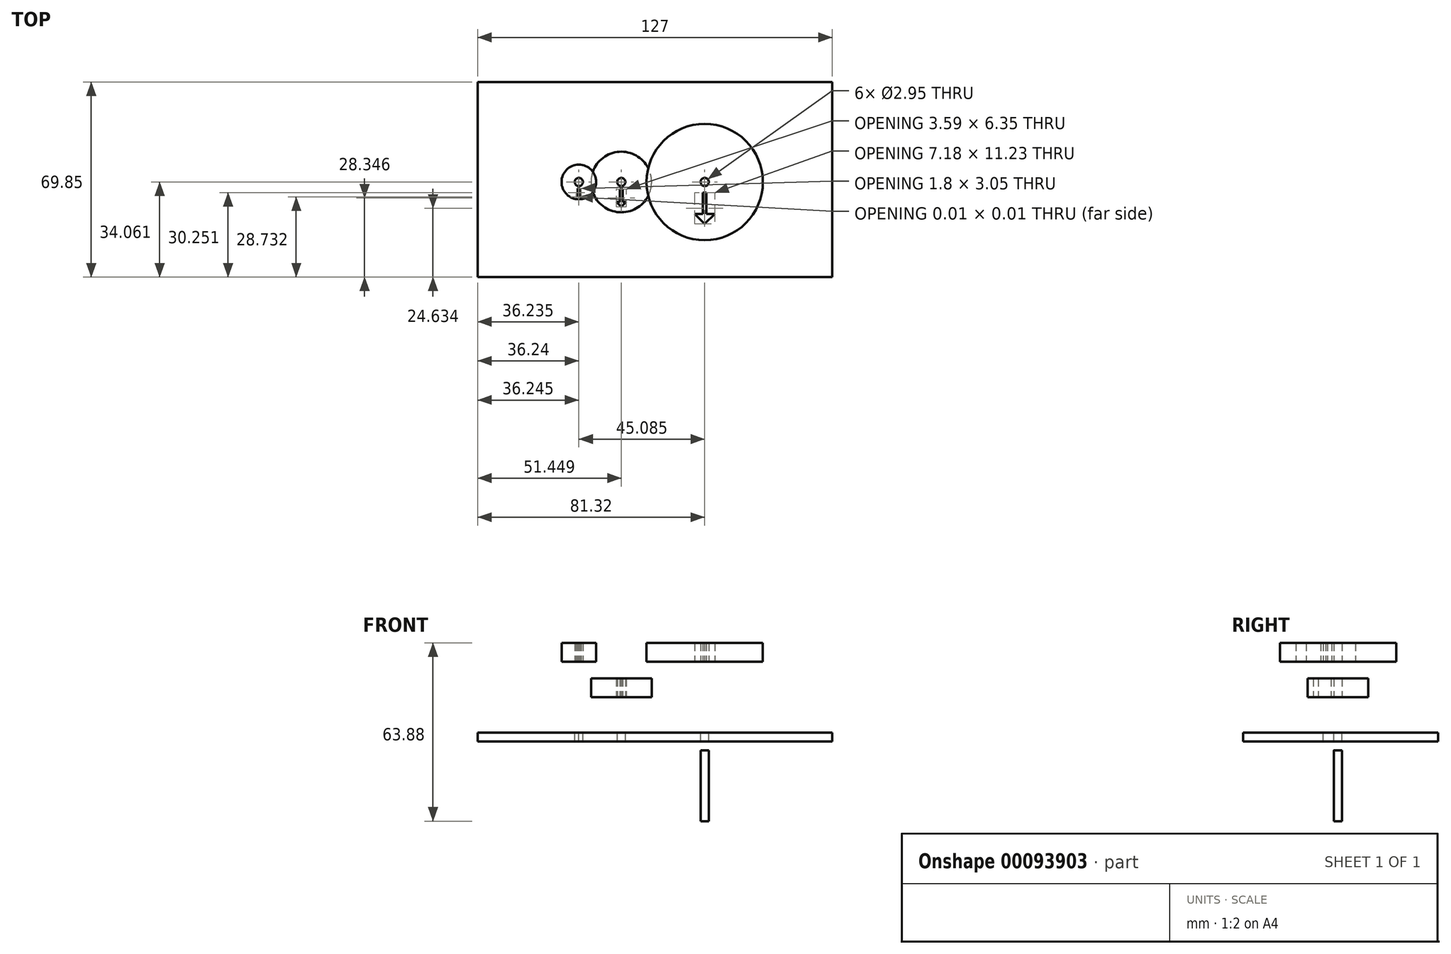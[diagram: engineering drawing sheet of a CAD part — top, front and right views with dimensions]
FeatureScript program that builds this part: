
annotation { "Feature Type Name" : "Feature", "Feature Type Description" : "" }
export const myFeature = defineFeature(function(context is Context, id is Id, definition is map)
    precondition{}
    {
        {
            var Q0;
            Q0=qCreatedBy(makeId("Top.planeOp"),FACE);
            var sketch = newSketch(context, id + "F0", { "sketchPlane" : qUnion([Q0])});
            skLineSegment(sketch, "E0", {"start": v(-33.34, 3.44) * mm, "end": v(-18.12, 3.44) * mm});
            skLineSegment(sketch, "E1", {"start": v(-18.12, 3.44) * mm, "end": v(11.75, 3.44) * mm});
            skCircle(sketch, "E2", {"center": v(-33.34, 3.44) * mm, "radius": 6.2 * mm});
            skCircle(sketch, "E3", {"center": v(11.75, 3.44) * mm, "radius": 20.84 * mm});
            skCircle(sketch, "E4", {"center": v(-18.12, 3.44) * mm, "radius": 10.86 * mm});
            skLineSegment(sketch, "E5.bottom", {"start": v(-69.57, 39.23) * mm, "end": v(57.43, 39.23) * mm});
            skLineSegment(sketch, "E5.top", {"start": v(-69.57, -30.62) * mm, "end": v(57.43, -30.62) * mm});
            skLineSegment(sketch, "E5.left", {"start": v(-69.57, 39.23) * mm, "end": v(-69.57, -30.62) * mm});
            skLineSegment(sketch, "E5.right", {"start": v(57.43, 39.23) * mm, "end": v(57.43, -30.62) * mm});
            skCircle(sketch, "E6", {"center": v(11.75, 3.44) * mm, "radius": 1.47 * mm});
            skCircle(sketch, "E7", {"center": v(-18.12, 3.44) * mm, "radius": 1.47 * mm});
            skCircle(sketch, "E8", {"center": v(-33.34, 3.44) * mm, "radius": 1.47 * mm});
            skLineSegment(sketch, "E9", {"start": v(11.75, 3.44) * mm, "end": v(11.75, -17.4) * mm});
            skLineSegment(sketch, "E10", {"start": v(11.11, -0.37) * mm, "end": v(11.11, -11.6) * mm});
            skLineSegment(sketch, "E11", {"start": v(11.11, -11.6) * mm, "end": v(12.38, -11.6) * mm});
            skLineSegment(sketch, "E12", {"start": v(11.11, -0.37) * mm, "end": v(12.38, -0.37) * mm});
            skLineSegment(sketch, "E13", {"start": v(12.38, -0.37) * mm, "end": v(12.38, -11.6) * mm});
            skLineSegment(sketch, "E14", {"start": v(11.75, -11.6) * mm, "end": v(15.34, -8) * mm});
            skLineSegment(sketch, "E15", {"start": v(11.75, -11.6) * mm, "end": v(8.16, -8) * mm});
            skLineSegment(sketch, "E16", {"start": v(8.16, -8) * mm, "end": v(15.34, -8) * mm});
            skLineSegment(sketch, "E17", {"start": v(-18.63, 0.9) * mm, "end": v(-18.63, -5.45) * mm});
            skLineSegment(sketch, "E18", {"start": v(-18.63, 0.9) * mm, "end": v(-17.61, 0.9) * mm});
            skLineSegment(sketch, "E19", {"start": v(-17.61, 0.9) * mm, "end": v(-17.61, -5.45) * mm});
            skLineSegment(sketch, "E20", {"start": v(-18.12, 3.44) * mm, "end": v(-18.12, -7.42) * mm});
            skLineSegment(sketch, "E21", {"start": v(-18.63, -5.45) * mm, "end": v(-17.61, -5.45) * mm});
            skLineSegment(sketch, "E22", {"start": v(-18.12, -5.45) * mm, "end": v(-16.32, -3.65) * mm});
            skLineSegment(sketch, "E23", {"start": v(-18.12, -5.45) * mm, "end": v(-19.92, -3.65) * mm});
            skLineSegment(sketch, "E24", {"start": v(-19.92, -3.65) * mm, "end": v(-16.32, -3.65) * mm});
            skLineSegment(sketch, "E25", {"start": v(-33.34, 3.44) * mm, "end": v(-33.34, -2.76) * mm});
            skLineSegment(sketch, "E26", {"start": v(-33.72, 1.15) * mm, "end": v(-32.95, 1.15) * mm});
            skLineSegment(sketch, "E27", {"start": v(-32.95, 1.15) * mm, "end": v(-32.95, -1.9) * mm});
            skLineSegment(sketch, "E28", {"start": v(-33.72, 1.15) * mm, "end": v(-33.72, -1.19) * mm});
            skLineSegment(sketch, "E29", {"start": v(-32.95, -1.9) * mm, "end": v(-33.7, -1.9) * mm});
            skLineSegment(sketch, "E30", {"start": v(-33.32, -1.9) * mm, "end": v(-32.43, -1) * mm});
            skLineSegment(sketch, "E31", {"start": v(-33.32, -1.9) * mm, "end": v(-34.22, -1) * mm});
            skLineSegment(sketch, "E32", {"start": v(-34.22, -1) * mm, "end": v(-32.43, -1) * mm});
            skSolve(sketch);
        }
        {
            var Q0;
            Q0=makeQuery(id+"F0.imprint","IMPRINT",FACE,{"disambiguationData":[TD([[makeQuery(id+"F0.imprint","IMPRINT",EDGE,{"derivedFrom":sQuery(id+"F0.wireOp",EDGE,"E5.bottom")}),-1.0]])]});
            var Q1;
            Q1=makeQuery(id+"F0.imprint","IMPRINT",FACE,{"disambiguationData":[TD([[makeQuery(id+"F0.imprint","IMPRINT",EDGE,{"derivedFrom":sQuery(id+"F0.wireOp",EDGE,"E6")}),-1.0]])]});
            var Q2;
            {var subQ6=sQuery(id+"F0.wireOp",EDGE,"E0");var subQ9=sQuery(id+"F0.wireOp",EDGE,"E2");var subQ10=makeQuery(id+"F0.imprint","INTERSECT",VERTEX,{"derivedFrom":[subQ6,subQ9]});Q2=makeQuery(id+"F0.imprint","IMPRINT",FACE,{"disambiguationData":[TD([[makeQuery(id+"F0.imprint","IMPRINT",EDGE,{"disambiguationData":[TD([[subQ10,-1.0]])],"derivedFrom":subQ6}),1.0]])]});}
            var Q3;
            Q3=makeQuery(id+"F0.imprint","IMPRINT",FACE,{"disambiguationData":[TD([[makeQuery(id+"F0.imprint","IMPRINT",EDGE,{"derivedFrom":sQuery(id+"F0.wireOp",EDGE,"E8")}),-1.0]])]});
            var Q4;
            {var subQ0=sQuery(id+"F0.wireOp",EDGE,"E4");var subQ1=sQuery(id+"F0.wireOp",EDGE,"E0");var subQ2=makeQuery(id+"F0.imprint","INTERSECT",VERTEX,{"derivedFrom":[subQ1,subQ0]});Q4=makeQuery(id+"F0.imprint","IMPRINT",FACE,{"disambiguationData":[TD([[makeQuery(id+"F0.imprint","IMPRINT",EDGE,{"disambiguationData":[TD([[subQ2,-1.0]])],"derivedFrom":subQ1}),-1.0]])]});}
            var Q5;
            {var subQ0=sQuery(id+"F0.wireOp",EDGE,"E4");var subQ1=sQuery(id+"F0.wireOp",EDGE,"E0");var subQ2=makeQuery(id+"F0.imprint","INTERSECT",VERTEX,{"derivedFrom":[subQ1,subQ0]});Q5=makeQuery(id+"F0.imprint","IMPRINT",FACE,{"disambiguationData":[TD([[makeQuery(id+"F0.imprint","IMPRINT",EDGE,{"disambiguationData":[TD([[subQ2,-1.0]])],"derivedFrom":subQ1}),1.0]])]});}
            var Q6;
            {var subQ0=sQuery(id+"F0.wireOp",EDGE,"E4");var subQ1=sQuery(id+"F0.wireOp",EDGE,"E1");var subQ2=makeQuery(id+"F0.imprint","INTERSECT",VERTEX,{"derivedFrom":[subQ1,subQ0]});Q6=makeQuery(id+"F0.imprint","IMPRINT",FACE,{"disambiguationData":[TD([[makeQuery(id+"F0.imprint","IMPRINT",EDGE,{"disambiguationData":[TD([[subQ2,1.0]])],"derivedFrom":subQ1}),-1.0]])]});}
            var Q7;
            {var subQ0=sQuery(id+"F0.wireOp",EDGE,"E4");var subQ1=sQuery(id+"F0.wireOp",EDGE,"E1");var subQ2=makeQuery(id+"F0.imprint","INTERSECT",VERTEX,{"derivedFrom":[subQ1,subQ0]});Q7=makeQuery(id+"F0.imprint","IMPRINT",FACE,{"disambiguationData":[TD([[makeQuery(id+"F0.imprint","IMPRINT",EDGE,{"disambiguationData":[TD([[subQ2,1.0]])],"derivedFrom":subQ1}),1.0]])]});}
            var Q8;
            {var subQ0=sQuery(id+"F0.wireOp",EDGE,"E26");var subQ1=sQuery(id+"F0.wireOp",EDGE,"E25");var subQ2=makeQuery(id+"F0.imprint","INTERSECT",VERTEX,{"derivedFrom":[subQ1,subQ0]});Q8=makeQuery(id+"F0.imprint","IMPRINT",FACE,{"disambiguationData":[TD([[makeQuery(id+"F0.imprint","IMPRINT",EDGE,{"disambiguationData":[TD([[subQ2,-1.0]])],"derivedFrom":subQ1}),-1.0]])]});}
            var Q9;
            {var subQ0=sQuery(id+"F0.wireOp",EDGE,"E32");var subQ1=sQuery(id+"F0.wireOp",EDGE,"E25");var subQ2=makeQuery(id+"F0.imprint","INTERSECT",VERTEX,{"derivedFrom":[subQ1,subQ0]});Q9=makeQuery(id+"F0.imprint","IMPRINT",FACE,{"disambiguationData":[TD([[makeQuery(id+"F0.imprint","IMPRINT",EDGE,{"disambiguationData":[TD([[subQ2,-1.0]])],"derivedFrom":subQ1}),-1.0]])]});}
            var Q10;
            {var subQ0=sQuery(id+"F0.wireOp",EDGE,"E26");var subQ1=sQuery(id+"F0.wireOp",EDGE,"E25");var subQ2=makeQuery(id+"F0.imprint","INTERSECT",VERTEX,{"derivedFrom":[subQ1,subQ0]});Q10=makeQuery(id+"F0.imprint","IMPRINT",FACE,{"disambiguationData":[TD([[makeQuery(id+"F0.imprint","IMPRINT",EDGE,{"disambiguationData":[TD([[subQ2,-1.0]])],"derivedFrom":subQ1}),1.0]])]});}
            var Q11;
            {var subQ5=sQuery(id+"F0.wireOp",EDGE,"E32");var subQ7=sQuery(id+"F0.wireOp",EDGE,"E25");var subQ9=makeQuery(id+"F0.imprint","INTERSECT",VERTEX,{"derivedFrom":[subQ7,subQ5]});Q11=makeQuery(id+"F0.imprint","IMPRINT",FACE,{"disambiguationData":[TD([[makeQuery(id+"F0.imprint","IMPRINT",EDGE,{"disambiguationData":[TD([[subQ9,-1.0]])],"derivedFrom":subQ7}),1.0]])]});}
            var Q12;
            {var subQ0=sQuery(id+"F0.wireOp",EDGE,"E32");var subQ1=sQuery(id+"F0.wireOp",EDGE,"E27");var subQ2=makeQuery(id+"F0.imprint","INTERSECT",VERTEX,{"derivedFrom":[subQ1,subQ0]});Q12=makeQuery(id+"F0.imprint","IMPRINT",FACE,{"disambiguationData":[TD([[makeQuery(id+"F0.imprint","IMPRINT",EDGE,{"disambiguationData":[TD([[subQ2,-1.0]])],"derivedFrom":subQ1}),1.0]])]});}
            var Q13;
            {var subQ0=sQuery(id+"F0.wireOp",EDGE,"E29");var subQ1=sQuery(id+"F0.wireOp",EDGE,"E27");var subQ2=makeQuery(id+"F0.imprint","INTERSECT",VERTEX,{"derivedFrom":[subQ1,subQ0]});Q13=makeQuery(id+"F0.imprint","IMPRINT",FACE,{"disambiguationData":[TD([[makeQuery(id+"F0.imprint","IMPRINT",EDGE,{"disambiguationData":[TD([[subQ2,1.0]])],"derivedFrom":subQ1}),-1.0]])]});}
            var Q14;
            {var subQ15=sQuery(id+"F0.wireOp",EDGE,"E8");var subQ20=sQuery(id+"F0.wireOp",EDGE,"E0");var subQ21=makeQuery(id+"F0.imprint","INTERSECT",VERTEX,{"derivedFrom":[subQ20,subQ15]});Q14=makeQuery(id+"F0.imprint","IMPRINT",FACE,{"disambiguationData":[TD([[makeQuery(id+"F0.imprint","IMPRINT",EDGE,{"disambiguationData":[TD([[subQ21,-1.0]])],"derivedFrom":subQ20}),-1.0]])]});}
            var Q15;
            {var subQ1=sQuery(id+"F0.wireOp",EDGE,"E7");var subQ15=sQuery(id+"F0.wireOp",EDGE,"E1");var subQ20=makeQuery(id+"F0.imprint","INTERSECT",VERTEX,{"derivedFrom":[subQ15,subQ1]});Q15=makeQuery(id+"F0.imprint","IMPRINT",FACE,{"disambiguationData":[TD([[makeQuery(id+"F0.imprint","IMPRINT",EDGE,{"disambiguationData":[TD([[subQ20,-1.0]])],"derivedFrom":subQ15}),-1.0]])]});}
            var Q16;
            {var subQ0=sQuery(id+"F0.wireOp",EDGE,"E18");var subQ1=sQuery(id+"F0.wireOp",EDGE,"E17");var subQ2=makeQuery(id+"F0.imprint","INTERSECT",VERTEX,{"derivedFrom":[subQ1,subQ0]});Q16=makeQuery(id+"F0.imprint","IMPRINT",FACE,{"disambiguationData":[TD([[makeQuery(id+"F0.imprint","IMPRINT",EDGE,{"disambiguationData":[TD([[subQ2,-1.0]])],"derivedFrom":subQ1}),1.0]])]});}
            var Q17;
            {var subQ0=sQuery(id+"F0.wireOp",EDGE,"E19");var subQ1=sQuery(id+"F0.wireOp",EDGE,"E18");var subQ2=makeQuery(id+"F0.imprint","INTERSECT",VERTEX,{"derivedFrom":[subQ1,subQ0]});Q17=makeQuery(id+"F0.imprint","IMPRINT",FACE,{"disambiguationData":[TD([[makeQuery(id+"F0.imprint","IMPRINT",EDGE,{"disambiguationData":[TD([[subQ2,1.0]])],"derivedFrom":subQ1}),-1.0]])]});}
            var Q18;
            {var subQ0=sQuery(id+"F0.wireOp",EDGE,"E24");var subQ1=sQuery(id+"F0.wireOp",EDGE,"E17");var subQ2=makeQuery(id+"F0.imprint","INTERSECT",VERTEX,{"derivedFrom":[subQ1,subQ0]});Q18=makeQuery(id+"F0.imprint","IMPRINT",FACE,{"disambiguationData":[TD([[makeQuery(id+"F0.imprint","IMPRINT",EDGE,{"disambiguationData":[TD([[subQ2,-1.0]])],"derivedFrom":subQ1}),-1.0]])]});}
            var Q19;
            {var subQ0=sQuery(id+"F0.wireOp",EDGE,"E24");var subQ1=sQuery(id+"F0.wireOp",EDGE,"E17");var subQ2=makeQuery(id+"F0.imprint","INTERSECT",VERTEX,{"derivedFrom":[subQ1,subQ0]});Q19=makeQuery(id+"F0.imprint","IMPRINT",FACE,{"disambiguationData":[TD([[makeQuery(id+"F0.imprint","IMPRINT",EDGE,{"disambiguationData":[TD([[subQ2,-1.0]])],"derivedFrom":subQ1}),1.0]])]});}
            var Q20;
            {var subQ0=sQuery(id+"F0.wireOp",EDGE,"E24");var subQ1=sQuery(id+"F0.wireOp",EDGE,"E19");var subQ2=makeQuery(id+"F0.imprint","INTERSECT",VERTEX,{"derivedFrom":[subQ1,subQ0]});Q20=makeQuery(id+"F0.imprint","IMPRINT",FACE,{"disambiguationData":[TD([[makeQuery(id+"F0.imprint","IMPRINT",EDGE,{"disambiguationData":[TD([[subQ2,-1.0]])],"derivedFrom":subQ1}),-1.0]])]});}
            var Q21;
            {var subQ0=sQuery(id+"F0.wireOp",EDGE,"E24");var subQ1=sQuery(id+"F0.wireOp",EDGE,"E19");var subQ2=makeQuery(id+"F0.imprint","INTERSECT",VERTEX,{"derivedFrom":[subQ1,subQ0]});Q21=makeQuery(id+"F0.imprint","IMPRINT",FACE,{"disambiguationData":[TD([[makeQuery(id+"F0.imprint","IMPRINT",EDGE,{"disambiguationData":[TD([[subQ2,-1.0]])],"derivedFrom":subQ1}),1.0]])]});}
            var Q22;
            {var subQ0=sQuery(id+"F0.wireOp",EDGE,"E21");var subQ1=sQuery(id+"F0.wireOp",EDGE,"E19");var subQ2=makeQuery(id+"F0.imprint","INTERSECT",VERTEX,{"derivedFrom":[subQ1,subQ0]});Q22=makeQuery(id+"F0.imprint","IMPRINT",FACE,{"disambiguationData":[TD([[makeQuery(id+"F0.imprint","IMPRINT",EDGE,{"disambiguationData":[TD([[subQ2,1.0]])],"derivedFrom":subQ1}),-1.0]])]});}
            var Q23;
            {var subQ0=sQuery(id+"F0.wireOp",EDGE,"E21");var subQ1=sQuery(id+"F0.wireOp",EDGE,"E17");var subQ2=makeQuery(id+"F0.imprint","INTERSECT",VERTEX,{"derivedFrom":[subQ1,subQ0]});Q23=makeQuery(id+"F0.imprint","IMPRINT",FACE,{"disambiguationData":[TD([[makeQuery(id+"F0.imprint","IMPRINT",EDGE,{"disambiguationData":[TD([[subQ2,1.0]])],"derivedFrom":subQ1}),1.0]])]});}
            var Q24;
            {var subQ7=sQuery(id+"F0.wireOp",EDGE,"E2");var subQ8=sQuery(id+"F0.wireOp",EDGE,"E0");var subQ9=makeQuery(id+"F0.imprint","INTERSECT",VERTEX,{"derivedFrom":[subQ8,subQ7]});Q24=makeQuery(id+"F0.imprint","IMPRINT",FACE,{"disambiguationData":[TD([[makeQuery(id+"F0.imprint","IMPRINT",EDGE,{"disambiguationData":[TD([[subQ9,-1.0]])],"derivedFrom":subQ8}),-1.0]])]});}
            var Q25;
            {var subQ3=sQuery(id+"F0.wireOp",EDGE,"E16");var subQ5=sQuery(id+"F0.wireOp",EDGE,"E13");var subQ6=makeQuery(id+"F0.imprint","INTERSECT",VERTEX,{"derivedFrom":[subQ5,subQ3]});Q25=makeQuery(id+"F0.imprint","IMPRINT",FACE,{"disambiguationData":[TD([[makeQuery(id+"F0.imprint","IMPRINT",EDGE,{"disambiguationData":[TD([[subQ6,-1.0]])],"derivedFrom":subQ5}),-1.0]])]});}
            var Q26;
            {var subQ0=sQuery(id+"F0.wireOp",EDGE,"E16");var subQ1=sQuery(id+"F0.wireOp",EDGE,"E13");var subQ2=makeQuery(id+"F0.imprint","INTERSECT",VERTEX,{"derivedFrom":[subQ1,subQ0]});Q26=makeQuery(id+"F0.imprint","IMPRINT",FACE,{"disambiguationData":[TD([[makeQuery(id+"F0.imprint","IMPRINT",EDGE,{"disambiguationData":[TD([[subQ2,-1.0]])],"derivedFrom":subQ1}),1.0]])]});}
            var Q27;
            {var subQ3=sQuery(id+"F0.wireOp",EDGE,"E16");var subQ5=sQuery(id+"F0.wireOp",EDGE,"E10");var subQ7=makeQuery(id+"F0.imprint","INTERSECT",VERTEX,{"derivedFrom":[subQ5,subQ3]});Q27=makeQuery(id+"F0.imprint","IMPRINT",FACE,{"disambiguationData":[TD([[makeQuery(id+"F0.imprint","IMPRINT",EDGE,{"disambiguationData":[TD([[subQ7,-1.0]])],"derivedFrom":subQ5}),1.0]])]});}
            var Q28;
            {var subQ0=sQuery(id+"F0.wireOp",EDGE,"E16");var subQ1=sQuery(id+"F0.wireOp",EDGE,"E10");var subQ2=makeQuery(id+"F0.imprint","INTERSECT",VERTEX,{"derivedFrom":[subQ1,subQ0]});Q28=makeQuery(id+"F0.imprint","IMPRINT",FACE,{"disambiguationData":[TD([[makeQuery(id+"F0.imprint","IMPRINT",EDGE,{"disambiguationData":[TD([[subQ2,-1.0]])],"derivedFrom":subQ1}),-1.0]])]});}
            var Q29;
            {var subQ0=sQuery(id+"F0.wireOp",EDGE,"E12");var subQ1=sQuery(id+"F0.wireOp",EDGE,"E9");var subQ2=makeQuery(id+"F0.imprint","INTERSECT",VERTEX,{"derivedFrom":[subQ1,subQ0]});Q29=makeQuery(id+"F0.imprint","IMPRINT",FACE,{"disambiguationData":[TD([[makeQuery(id+"F0.imprint","IMPRINT",EDGE,{"disambiguationData":[TD([[subQ2,-1.0]])],"derivedFrom":subQ1}),1.0]])]});}
            var Q30;
            {var subQ0=sQuery(id+"F0.wireOp",EDGE,"E12");var subQ1=sQuery(id+"F0.wireOp",EDGE,"E9");var subQ2=makeQuery(id+"F0.imprint","INTERSECT",VERTEX,{"derivedFrom":[subQ1,subQ0]});Q30=makeQuery(id+"F0.imprint","IMPRINT",FACE,{"disambiguationData":[TD([[makeQuery(id+"F0.imprint","IMPRINT",EDGE,{"disambiguationData":[TD([[subQ2,-1.0]])],"derivedFrom":subQ1}),-1.0]])]});}
            var Q31;
            {var subQ0=sQuery(id+"F0.wireOp",EDGE,"E13");var subQ1=sQuery(id+"F0.wireOp",EDGE,"E11");var subQ2=makeQuery(id+"F0.imprint","INTERSECT",VERTEX,{"derivedFrom":[subQ1,subQ0]});Q31=makeQuery(id+"F0.imprint","IMPRINT",FACE,{"disambiguationData":[TD([[makeQuery(id+"F0.imprint","IMPRINT",EDGE,{"disambiguationData":[TD([[subQ2,1.0]])],"derivedFrom":subQ0}),-1.0]])]});}
            var Q32;
            {var subQ0=sQuery(id+"F0.wireOp",EDGE,"E11");var subQ1=sQuery(id+"F0.wireOp",EDGE,"E10");var subQ2=makeQuery(id+"F0.imprint","INTERSECT",VERTEX,{"derivedFrom":[subQ1,subQ0]});Q32=makeQuery(id+"F0.imprint","IMPRINT",FACE,{"disambiguationData":[TD([[makeQuery(id+"F0.imprint","IMPRINT",EDGE,{"disambiguationData":[TD([[subQ2,1.0]])],"derivedFrom":subQ1}),1.0]])]});}
            extrude(context, id + "F1", {"entities" : qUnion([Q0, Q1, Q2, Q3, Q4, Q5, Q6, Q7, Q8, Q9, Q10, Q11, Q12, Q13, Q14, Q15, Q16, Q17, Q18, Q19, Q20, Q21, Q22, Q23, Q24, Q25, Q26, Q27, Q28, Q29, Q30, Q31, Q32]), "oppositeDirection" : true, "depth" : 3.17 * mm});
        }
        {
            var Q0;
            {var subQ7=sQuery(id+"F0.wireOp",EDGE,"E4");var subQ8=sQuery(id+"F0.wireOp",EDGE,"E1");var subQ9=makeQuery(id+"F0.imprint","INTERSECT",VERTEX,{"derivedFrom":[subQ8,subQ7]});Q0=makeQuery(id+"F0.imprint","IMPRINT",FACE,{"disambiguationData":[TD([[makeQuery(id+"F0.imprint","IMPRINT",EDGE,{"disambiguationData":[TD([[subQ9,-1.0]])],"derivedFrom":subQ8}),-1.0]])]});}
            var Q1;
            {var subQ0=sQuery(id+"F0.wireOp",EDGE,"E3");var subQ1=sQuery(id+"F0.wireOp",EDGE,"E1");var subQ2=makeQuery(id+"F0.imprint","INTERSECT",VERTEX,{"derivedFrom":[subQ1,subQ0]});Q1=makeQuery(id+"F0.imprint","IMPRINT",FACE,{"disambiguationData":[TD([[makeQuery(id+"F0.imprint","IMPRINT",EDGE,{"disambiguationData":[TD([[subQ2,-1.0]])],"derivedFrom":subQ1}),-1.0]])]});}
            var Q2;
            {var subQ0=sQuery(id+"F0.wireOp",EDGE,"E3");var subQ1=sQuery(id+"F0.wireOp",EDGE,"E1");var subQ2=makeQuery(id+"F0.imprint","INTERSECT",VERTEX,{"derivedFrom":[subQ1,subQ0]});Q2=makeQuery(id+"F0.imprint","IMPRINT",FACE,{"disambiguationData":[TD([[makeQuery(id+"F0.imprint","IMPRINT",EDGE,{"disambiguationData":[TD([[subQ2,-1.0]])],"derivedFrom":subQ1}),1.0]])]});}
            var Q3;
            {var subQ0=sQuery(id+"F0.wireOp",EDGE,"E13");var subQ1=sQuery(id+"F0.wireOp",EDGE,"E11");var subQ2=makeQuery(id+"F0.imprint","INTERSECT",VERTEX,{"derivedFrom":[subQ1,subQ0]});Q3=makeQuery(id+"F0.imprint","IMPRINT",FACE,{"disambiguationData":[TD([[makeQuery(id+"F0.imprint","IMPRINT",EDGE,{"disambiguationData":[TD([[subQ2,1.0]])],"derivedFrom":subQ0}),-1.0]])]});}
            var Q4;
            {var subQ0=sQuery(id+"F0.wireOp",EDGE,"E11");var subQ1=sQuery(id+"F0.wireOp",EDGE,"E10");var subQ2=makeQuery(id+"F0.imprint","INTERSECT",VERTEX,{"derivedFrom":[subQ1,subQ0]});Q4=makeQuery(id+"F0.imprint","IMPRINT",FACE,{"disambiguationData":[TD([[makeQuery(id+"F0.imprint","IMPRINT",EDGE,{"disambiguationData":[TD([[subQ2,1.0]])],"derivedFrom":subQ1}),1.0]])]});}
            var Q5;
            {var subQ15=sQuery(id+"F0.wireOp",EDGE,"E4");var subQ16=sQuery(id+"F0.wireOp",EDGE,"E1");var subQ17=makeQuery(id+"F0.imprint","INTERSECT",VERTEX,{"derivedFrom":[subQ16,subQ15]});Q5=makeQuery(id+"F0.imprint","IMPRINT",FACE,{"disambiguationData":[TD([[makeQuery(id+"F0.imprint","IMPRINT",EDGE,{"disambiguationData":[TD([[subQ17,-1.0]])],"derivedFrom":subQ16}),1.0]])]});}
            extrude(context, id + "F2", {"entities" : qUnion([Q0, Q1, Q2, Q3, Q4, Q5]), "depth" : 32.13 * mm, "hasSecondDirection" : true, "secondDirectionOppositeDirection" : false, "secondDirectionDepth" : 25.4 * mm});
        }
        {
            var Q0;
            {var subQ0=sQuery(id+"F0.wireOp",EDGE,"E4");var subQ1=sQuery(id+"F0.wireOp",EDGE,"E0");var subQ2=makeQuery(id+"F0.imprint","INTERSECT",VERTEX,{"derivedFrom":[subQ1,subQ0]});Q0=makeQuery(id+"F0.imprint","IMPRINT",FACE,{"disambiguationData":[TD([[makeQuery(id+"F0.imprint","IMPRINT",EDGE,{"disambiguationData":[TD([[subQ2,-1.0]])],"derivedFrom":subQ1}),1.0]])]});}
            var Q1;
            {var subQ0=sQuery(id+"F0.wireOp",EDGE,"E4");var subQ1=sQuery(id+"F0.wireOp",EDGE,"E0");var subQ2=makeQuery(id+"F0.imprint","INTERSECT",VERTEX,{"derivedFrom":[subQ1,subQ0]});Q1=makeQuery(id+"F0.imprint","IMPRINT",FACE,{"disambiguationData":[TD([[makeQuery(id+"F0.imprint","IMPRINT",EDGE,{"disambiguationData":[TD([[subQ2,-1.0]])],"derivedFrom":subQ1}),-1.0]])]});}
            var Q2;
            {var subQ13=sQuery(id+"F0.wireOp",EDGE,"E8");var subQ14=sQuery(id+"F0.wireOp",EDGE,"E0");var subQ15=makeQuery(id+"F0.imprint","INTERSECT",VERTEX,{"derivedFrom":[subQ14,subQ13]});Q2=makeQuery(id+"F0.imprint","IMPRINT",FACE,{"disambiguationData":[TD([[makeQuery(id+"F0.imprint","IMPRINT",EDGE,{"disambiguationData":[TD([[subQ15,-1.0]])],"derivedFrom":subQ14}),1.0]])]});}
            var Q3;
            {var subQ0=sQuery(id+"F0.wireOp",EDGE,"E29");var subQ1=sQuery(id+"F0.wireOp",EDGE,"E27");var subQ2=makeQuery(id+"F0.imprint","INTERSECT",VERTEX,{"derivedFrom":[subQ1,subQ0]});Q3=makeQuery(id+"F0.imprint","IMPRINT",FACE,{"disambiguationData":[TD([[makeQuery(id+"F0.imprint","IMPRINT",EDGE,{"disambiguationData":[TD([[subQ2,1.0]])],"derivedFrom":subQ1}),-1.0]])]});}
            var Q4;
            {var subQ15=sQuery(id+"F0.wireOp",EDGE,"E8");var subQ20=sQuery(id+"F0.wireOp",EDGE,"E0");var subQ21=makeQuery(id+"F0.imprint","INTERSECT",VERTEX,{"derivedFrom":[subQ20,subQ15]});Q4=makeQuery(id+"F0.imprint","IMPRINT",FACE,{"disambiguationData":[TD([[makeQuery(id+"F0.imprint","IMPRINT",EDGE,{"disambiguationData":[TD([[subQ21,-1.0]])],"derivedFrom":subQ20}),-1.0]])]});}
            extrude(context, id + "F3", {"entities" : qUnion([Q0, Q1, Q2, Q3, Q4]), "depth" : 32.13 * mm, "hasSecondDirection" : true, "secondDirectionOppositeDirection" : false, "secondDirectionDepth" : 25.4 * mm});
        }
        {
            var Q0;
            {var subQ0=sQuery(id+"F0.wireOp",EDGE,"E4");var subQ1=sQuery(id+"F0.wireOp",EDGE,"E1");var subQ2=makeQuery(id+"F0.imprint","INTERSECT",VERTEX,{"derivedFrom":[subQ1,subQ0]});Q0=makeQuery(id+"F0.imprint","IMPRINT",FACE,{"disambiguationData":[TD([[makeQuery(id+"F0.imprint","IMPRINT",EDGE,{"disambiguationData":[TD([[subQ2,1.0]])],"derivedFrom":subQ1}),1.0]])]});}
            var Q1;
            {var subQ0=sQuery(id+"F0.wireOp",EDGE,"E4");var subQ1=sQuery(id+"F0.wireOp",EDGE,"E1");var subQ2=makeQuery(id+"F0.imprint","INTERSECT",VERTEX,{"derivedFrom":[subQ1,subQ0]});Q1=makeQuery(id+"F0.imprint","IMPRINT",FACE,{"disambiguationData":[TD([[makeQuery(id+"F0.imprint","IMPRINT",EDGE,{"disambiguationData":[TD([[subQ2,1.0]])],"derivedFrom":subQ1}),-1.0]])]});}
            var Q2;
            {var subQ6=sQuery(id+"F0.wireOp",EDGE,"E0");var subQ9=sQuery(id+"F0.wireOp",EDGE,"E2");var subQ10=makeQuery(id+"F0.imprint","INTERSECT",VERTEX,{"derivedFrom":[subQ6,subQ9]});Q2=makeQuery(id+"F0.imprint","IMPRINT",FACE,{"disambiguationData":[TD([[makeQuery(id+"F0.imprint","IMPRINT",EDGE,{"disambiguationData":[TD([[subQ10,-1.0]])],"derivedFrom":subQ6}),1.0]])]});}
            var Q3;
            {var subQ5=sQuery(id+"F0.wireOp",EDGE,"E2");var subQ6=sQuery(id+"F0.wireOp",EDGE,"E0");var subQ7=makeQuery(id+"F0.imprint","INTERSECT",VERTEX,{"derivedFrom":[subQ6,subQ5]});Q3=makeQuery(id+"F0.imprint","IMPRINT",FACE,{"disambiguationData":[TD([[makeQuery(id+"F0.imprint","IMPRINT",EDGE,{"disambiguationData":[TD([[subQ7,-1.0]])],"derivedFrom":subQ6}),-1.0]])]});}
            var Q4;
            {var subQ0=sQuery(id+"F0.wireOp",EDGE,"E4");var subQ1=sQuery(id+"F0.wireOp",EDGE,"E0");var subQ2=makeQuery(id+"F0.imprint","INTERSECT",VERTEX,{"derivedFrom":[subQ1,subQ0]});Q4=makeQuery(id+"F0.imprint","IMPRINT",FACE,{"disambiguationData":[TD([[makeQuery(id+"F0.imprint","IMPRINT",EDGE,{"disambiguationData":[TD([[subQ2,-1.0]])],"derivedFrom":subQ1}),1.0]])]});}
            var Q5;
            {var subQ0=sQuery(id+"F0.wireOp",EDGE,"E4");var subQ1=sQuery(id+"F0.wireOp",EDGE,"E0");var subQ2=makeQuery(id+"F0.imprint","INTERSECT",VERTEX,{"derivedFrom":[subQ1,subQ0]});Q5=makeQuery(id+"F0.imprint","IMPRINT",FACE,{"disambiguationData":[TD([[makeQuery(id+"F0.imprint","IMPRINT",EDGE,{"disambiguationData":[TD([[subQ2,-1.0]])],"derivedFrom":subQ1}),-1.0]])]});}
            var Q6;
            {var subQ1=sQuery(id+"F0.wireOp",EDGE,"E7");var subQ15=sQuery(id+"F0.wireOp",EDGE,"E1");var subQ20=makeQuery(id+"F0.imprint","INTERSECT",VERTEX,{"derivedFrom":[subQ15,subQ1]});Q6=makeQuery(id+"F0.imprint","IMPRINT",FACE,{"disambiguationData":[TD([[makeQuery(id+"F0.imprint","IMPRINT",EDGE,{"disambiguationData":[TD([[subQ20,-1.0]])],"derivedFrom":subQ15}),-1.0]])]});}
            var Q7;
            {var subQ0=sQuery(id+"F0.wireOp",EDGE,"E21");var subQ1=sQuery(id+"F0.wireOp",EDGE,"E19");var subQ2=makeQuery(id+"F0.imprint","INTERSECT",VERTEX,{"derivedFrom":[subQ1,subQ0]});Q7=makeQuery(id+"F0.imprint","IMPRINT",FACE,{"disambiguationData":[TD([[makeQuery(id+"F0.imprint","IMPRINT",EDGE,{"disambiguationData":[TD([[subQ2,1.0]])],"derivedFrom":subQ1}),-1.0]])]});}
            var Q8;
            {var subQ0=sQuery(id+"F0.wireOp",EDGE,"E21");var subQ1=sQuery(id+"F0.wireOp",EDGE,"E17");var subQ2=makeQuery(id+"F0.imprint","INTERSECT",VERTEX,{"derivedFrom":[subQ1,subQ0]});Q8=makeQuery(id+"F0.imprint","IMPRINT",FACE,{"disambiguationData":[TD([[makeQuery(id+"F0.imprint","IMPRINT",EDGE,{"disambiguationData":[TD([[subQ2,1.0]])],"derivedFrom":subQ1}),1.0]])]});}
            extrude(context, id + "F4", {"entities" : qUnion([Q0, Q1, Q2, Q3, Q4, Q5, Q6, Q7, Q8]), "depth" : 19.43 * mm, "hasSecondDirection" : true, "secondDirectionOppositeDirection" : false, "secondDirectionDepth" : 12.7 * mm});
        }
        {
            var Q0;
            Q0=makeQuery(id+"F0.imprint","IMPRINT",FACE,{"disambiguationData":[TD([[makeQuery(id+"F0.imprint","IMPRINT",EDGE,{"derivedFrom":sQuery(id+"F0.wireOp",EDGE,"E6")}),1.0]])]});
            extrude(context, id + "F5", {"entities" : qUnion([Q0]), "oppositeDirection" : true, "depth" : 31.75 * mm, "hasSecondDirection" : true, "secondDirectionOppositeDirection" : true, "secondDirectionDepth" : 6.35 * mm});
        }
    });
